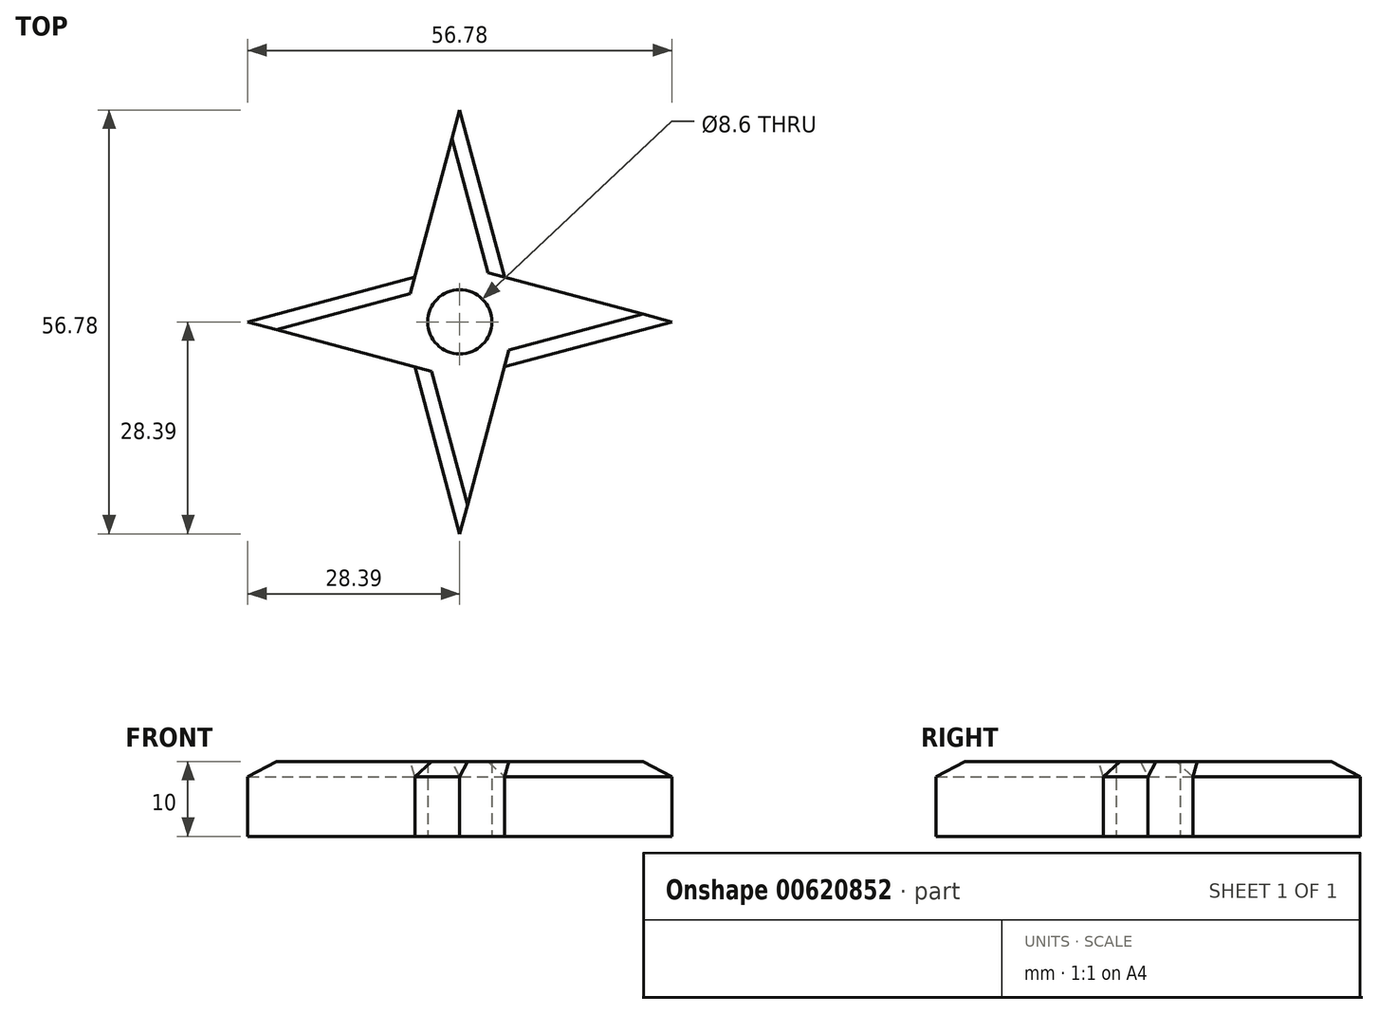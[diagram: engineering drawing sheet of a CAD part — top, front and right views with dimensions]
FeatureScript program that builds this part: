
annotation { "Feature Type Name" : "Feature", "Feature Type Description" : "" }
export const myFeature = defineFeature(function(context is Context, id is Id, definition is map)
    precondition{}
    {
        {
            var Q0;
            Q0=qCreatedBy(makeId("Top.planeOp"),FACE);
            var sketch = newSketch(context, id + "F0", { "sketchPlane" : qUnion([Q0])});
            skCircle(sketch, "E0", {"center": v(0, 0) * mm, "radius": 4.3 * mm});
            skLineSegment(sketch, "E1.bottom", {"start": v(6, -6) * mm, "end": v(-6, -6) * mm});
            skLineSegment(sketch, "E1.top", {"start": v(6, 6) * mm, "end": v(-6, 6) * mm});
            skLineSegment(sketch, "E1.left", {"start": v(6, -6) * mm, "end": v(6, 6) * mm});
            skLineSegment(sketch, "E1.right", {"start": v(-6, -6) * mm, "end": v(-6, 6) * mm});
            skLineSegment(sketch, "E2", {"start": v(6, -6) * mm, "end": v(28.4, 0) * mm});
            skLineSegment(sketch, "E3", {"start": v(28.4, 0) * mm, "end": v(6, 6) * mm});
            skLineSegment(sketch, "E4", {"start": v(-6, -6) * mm, "end": v(0, -28.4) * mm});
            skLineSegment(sketch, "E5", {"start": v(0, -28.4) * mm, "end": v(6, -6) * mm});
            skLineSegment(sketch, "E6", {"start": v(-6, 6) * mm, "end": v(0, 28.4) * mm});
            skLineSegment(sketch, "E7", {"start": v(0, 28.4) * mm, "end": v(6, 6) * mm});
            skLineSegment(sketch, "E8", {"start": v(-6, 6) * mm, "end": v(-28.4, 0) * mm});
            skLineSegment(sketch, "E9", {"start": v(-28.4, 0) * mm, "end": v(-6, -6) * mm});
            skSolve(sketch);
        }
        {
            var Q0;
            Q0=makeQuery(id+"F0.imprint","IMPRINT",FACE,{"disambiguationData":[TD([[makeQuery(id+"F0.imprint","IMPRINT",EDGE,{"derivedFrom":sQuery(id+"F0.wireOp",EDGE,"E1.bottom")}),1.0]])]});
            var Q1;
            Q1=makeQuery(id+"F0.imprint","IMPRINT",FACE,{"disambiguationData":[TD([[makeQuery(id+"F0.imprint","IMPRINT",EDGE,{"derivedFrom":sQuery(id+"F0.wireOp",EDGE,"E1.left")}),-1.0]])]});
            var Q2;
            Q2=makeQuery(id+"F0.imprint","IMPRINT",FACE,{"disambiguationData":[TD([[makeQuery(id+"F0.imprint","IMPRINT",EDGE,{"derivedFrom":sQuery(id+"F0.wireOp",EDGE,"E0")}),-1.0]])]});
            var Q3;
            Q3=makeQuery(id+"F0.imprint","IMPRINT",FACE,{"disambiguationData":[TD([[makeQuery(id+"F0.imprint","IMPRINT",EDGE,{"derivedFrom":sQuery(id+"F0.wireOp",EDGE,"E1.top")}),-1.0]])]});
            var Q4;
            Q4=makeQuery(id+"F0.imprint","IMPRINT",FACE,{"disambiguationData":[TD([[makeQuery(id+"F0.imprint","IMPRINT",EDGE,{"derivedFrom":sQuery(id+"F0.wireOp",EDGE,"E1.right")}),1.0]])]});
            extrude(context, id + "F1", {"entities" : qUnion([Q0, Q1, Q2, Q3, Q4]), "depth" : 10 * mm, "offsetDistance" : 25 * mm});
        }
        {
            var Q0;
            Q0=makeQuery(id+"F1.opExtrude","CAP_EDGE",EDGE,{"disambiguationData":[OSD([sQuery(id+"F0.wireOp",EDGE,"E4")])],"isStart":false});
            var Q1;
            Q1=makeQuery(id+"F1.opExtrude","CAP_EDGE",EDGE,{"disambiguationData":[OSD([sQuery(id+"F0.wireOp",EDGE,"E8")])],"isStart":false});
            var Q2;
            Q2=makeQuery(id+"F1.opExtrude","CAP_EDGE",EDGE,{"disambiguationData":[OSD([sQuery(id+"F0.wireOp",EDGE,"E7")])],"isStart":false});
            var Q3;
            Q3=makeQuery(id+"F1.opExtrude","CAP_EDGE",EDGE,{"disambiguationData":[OSD([sQuery(id+"F0.wireOp",EDGE,"E2")])],"isStart":false});
            chamfer(context, id + "F2", {"entities" : qUnion([Q0, Q1, Q2, Q3]), "width" : 2 * mm, "tangentPropagation" : true});
        }
    });
